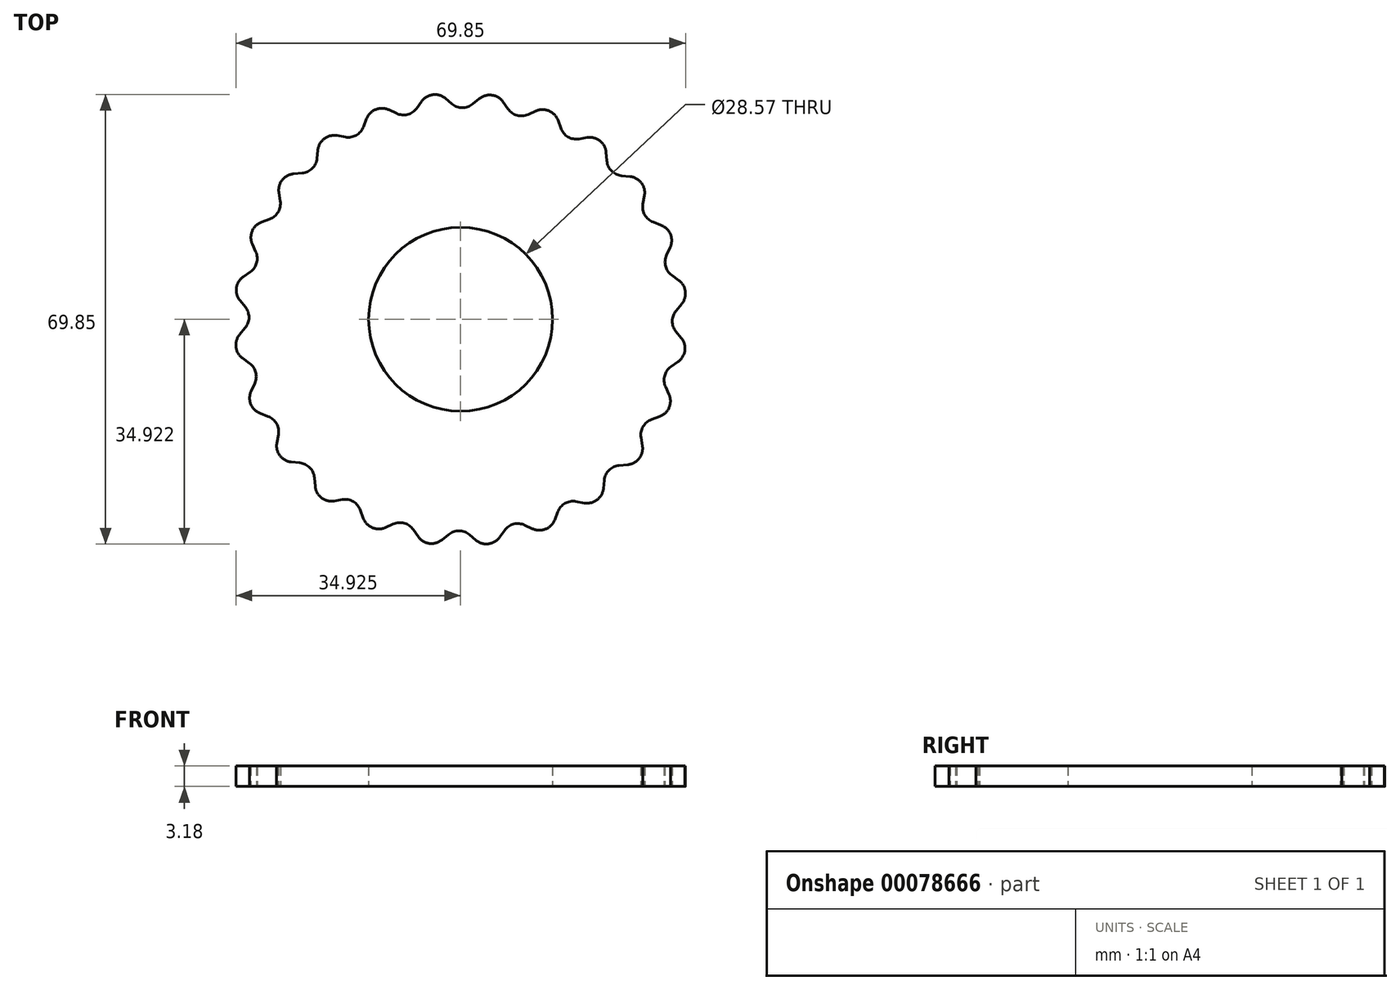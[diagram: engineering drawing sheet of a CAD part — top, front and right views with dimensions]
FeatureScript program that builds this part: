
annotation { "Feature Type Name" : "Feature", "Feature Type Description" : "" }
export const myFeature = defineFeature(function(context is Context, id is Id, definition is map)
    precondition{}
    {
        {
            var Q0;
            Q0=qCreatedBy(makeId("Top.planeOp"),FACE);
            var sketch = newSketch(context, id + "F0", { "sketchPlane" : qUnion([Q0])});
            skLineSegment(sketch, "E0", {"start": v(-103.02, 36.58) * mm, "end": v(-101.72, 36.35) * mm});
            skLineSegment(sketch, "E1", {"start": v(-98.9, 37.94) * mm, "end": v(-98.43, 39.18) * mm});
            skPoint(sketch, "E2.visualSharp", {"position": v(-99.65, 35.98) * mm});
            skArc(sketch, "E2.filletArc", {"start": v(-101.72, 36.35) * mm, "mid": v(-100.02, 36.64) * mm, "end": v(-98.9, 37.94) * mm});
            skPoint(sketch, "E3.1.0", {"position": v(-106.35, 30.93) * mm});
            skLineSegment(sketch, "E3.1.1", {"start": v(-109.76, 30.63) * mm, "end": v(-108.44, 30.75) * mm});
            skLineSegment(sketch, "E3.1.5", {"start": v(-106.13, 33.02) * mm, "end": v(-106, 34.34) * mm});
            skArc(sketch, "E3.1.6", {"start": v(-108.44, 30.75) * mm, "mid": v(-106.88, 31.47) * mm, "end": v(-106.13, 33.02) * mm});
            skPoint(sketch, "E3.2.0", {"position": v(-111.5, 24.32) * mm});
            skLineSegment(sketch, "E3.2.1", {"start": v(-114.72, 23.15) * mm, "end": v(-113.48, 23.6) * mm});
            skLineSegment(sketch, "E3.2.5", {"start": v(-111.84, 26.4) * mm, "end": v(-112.05, 27.7) * mm});
            skArc(sketch, "E3.2.6", {"start": v(-113.48, 23.6) * mm, "mid": v(-112.16, 24.7) * mm, "end": v(-111.84, 26.4) * mm});
            skPoint(sketch, "E3.3.0", {"position": v(-114.78, 16.6) * mm});
            skLineSegment(sketch, "E3.3.1", {"start": v(-117.58, 14.63) * mm, "end": v(-116.5, 15.4) * mm});
            skLineSegment(sketch, "E3.3.5", {"start": v(-115.63, 18.51) * mm, "end": v(-116.18, 19.72) * mm});
            skArc(sketch, "E3.3.6", {"start": v(-116.5, 15.4) * mm, "mid": v(-115.5, 16.8) * mm, "end": v(-115.63, 18.51) * mm});
            skPoint(sketch, "E3.4.0", {"position": v(-115.94, 8.3) * mm});
            skLineSegment(sketch, "E3.4.1", {"start": v(-118.14, 5.67) * mm, "end": v(-117.29, 6.68) * mm});
            skLineSegment(sketch, "E3.4.5", {"start": v(-117.26, 9.92) * mm, "end": v(-118.1, 10.95) * mm});
            skArc(sketch, "E3.4.6", {"start": v(-117.29, 6.68) * mm, "mid": v(-116.7, 8.3) * mm, "end": v(-117.26, 9.92) * mm});
            skPoint(sketch, "E3.5.0", {"position": v(-114.9, -0.03) * mm});
            skLineSegment(sketch, "E3.5.1", {"start": v(-116.36, -3.13) * mm, "end": v(-115.8, -1.93) * mm});
            skLineSegment(sketch, "E3.5.5", {"start": v(-116.61, 1.2) * mm, "end": v(-117.69, 1.98) * mm});
            skArc(sketch, "E3.5.6", {"start": v(-115.8, -1.93) * mm, "mid": v(-115.64, -0.22) * mm, "end": v(-116.61, 1.2) * mm});
            skPoint(sketch, "E3.6.0", {"position": v(-111.76, -7.8) * mm});
            skLineSegment(sketch, "E3.6.1", {"start": v(-112.36, -11.18) * mm, "end": v(-112.13, -9.87) * mm});
            skLineSegment(sketch, "E3.6.5", {"start": v(-113.73, -7.06) * mm, "end": v(-114.96, -6.58) * mm});
            skArc(sketch, "E3.6.6", {"start": v(-112.13, -9.87) * mm, "mid": v(-112.42, -8.18) * mm, "end": v(-113.73, -7.06) * mm});
            skPoint(sketch, "E3.7.0", {"position": v(-106.71, -14.5) * mm});
            skLineSegment(sketch, "E3.7.1", {"start": v(-106.42, -17.91) * mm, "end": v(-106.53, -16.6) * mm});
            skLineSegment(sketch, "E3.7.5", {"start": v(-108.8, -14.28) * mm, "end": v(-110.12, -14.15) * mm});
            skArc(sketch, "E3.7.6", {"start": v(-106.53, -16.6) * mm, "mid": v(-107.25, -15.03) * mm, "end": v(-108.8, -14.28) * mm});
            skPoint(sketch, "E3.8.0", {"position": v(-100.1, -19.66) * mm});
            skLineSegment(sketch, "E3.8.1", {"start": v(-98.93, -22.88) * mm, "end": v(-99.38, -21.63) * mm});
            skLineSegment(sketch, "E3.8.5", {"start": v(-102.17, -20) * mm, "end": v(-103.48, -20.2) * mm});
            skArc(sketch, "E3.8.6", {"start": v(-99.38, -21.63) * mm, "mid": v(-100.48, -20.3) * mm, "end": v(-102.17, -20) * mm});
            skPoint(sketch, "E3.9.0", {"position": v(-92.38, -22.93) * mm});
            skLineSegment(sketch, "E3.9.1", {"start": v(-90.42, -25.74) * mm, "end": v(-91.17, -24.65) * mm});
            skLineSegment(sketch, "E3.9.5", {"start": v(-94.3, -23.79) * mm, "end": v(-95.5, -24.33) * mm});
            skArc(sketch, "E3.9.6", {"start": v(-91.17, -24.65) * mm, "mid": v(-92.58, -23.66) * mm, "end": v(-94.3, -23.79) * mm});
            skPoint(sketch, "E3.10.0", {"position": v(-84.07, -24.09) * mm});
            skLineSegment(sketch, "E3.10.1", {"start": v(-81.45, -26.3) * mm, "end": v(-82.47, -25.44) * mm});
            skLineSegment(sketch, "E3.10.5", {"start": v(-85.7, -25.42) * mm, "end": v(-86.73, -26.25) * mm});
            skArc(sketch, "E3.10.6", {"start": v(-82.47, -25.44) * mm, "mid": v(-84.08, -24.85) * mm, "end": v(-85.7, -25.42) * mm});
            skPoint(sketch, "E3.11.0", {"position": v(-75.75, -23.06) * mm});
            skLineSegment(sketch, "E3.11.1", {"start": v(-72.65, -24.51) * mm, "end": v(-73.85, -23.95) * mm});
            skLineSegment(sketch, "E3.11.5", {"start": v(-76.98, -24.76) * mm, "end": v(-77.76, -25.84) * mm});
            skArc(sketch, "E3.11.6", {"start": v(-73.85, -23.95) * mm, "mid": v(-75.56, -23.8) * mm, "end": v(-76.98, -24.76) * mm});
            skPoint(sketch, "E3.12.0", {"position": v(-67.98, -19.92) * mm});
            skLineSegment(sketch, "E3.12.1", {"start": v(-64.6, -20.51) * mm, "end": v(-65.9, -20.28) * mm});
            skLineSegment(sketch, "E3.12.5", {"start": v(-68.73, -21.88) * mm, "end": v(-69.2, -23.12) * mm});
            skArc(sketch, "E3.12.6", {"start": v(-65.9, -20.28) * mm, "mid": v(-67.6, -20.57) * mm, "end": v(-68.73, -21.88) * mm});
            skPoint(sketch, "E3.13.0", {"position": v(-61.28, -14.86) * mm});
            skLineSegment(sketch, "E3.13.1", {"start": v(-57.87, -14.57) * mm, "end": v(-59.2, -14.68) * mm});
            skLineSegment(sketch, "E3.13.5", {"start": v(-61.5, -16.95) * mm, "end": v(-61.63, -18.27) * mm});
            skArc(sketch, "E3.13.6", {"start": v(-59.2, -14.68) * mm, "mid": v(-60.75, -15.4) * mm, "end": v(-61.5, -16.95) * mm});
            skPoint(sketch, "E3.14.0", {"position": v(-56.13, -8.25) * mm});
            skLineSegment(sketch, "E3.14.1", {"start": v(-52.9, -7.08) * mm, "end": v(-54.15, -7.54) * mm});
            skLineSegment(sketch, "E3.14.5", {"start": v(-55.8, -10.33) * mm, "end": v(-55.58, -11.64) * mm});
            skArc(sketch, "E3.14.6", {"start": v(-54.15, -7.54) * mm, "mid": v(-55.47, -8.64) * mm, "end": v(-55.8, -10.33) * mm});
            skPoint(sketch, "E3.15.0", {"position": v(-52.85, -0.53) * mm});
            skLineSegment(sketch, "E3.15.1", {"start": v(-50.05, 1.43) * mm, "end": v(-51.13, 0.67) * mm});
            skLineSegment(sketch, "E3.15.5", {"start": v(-52, -2.45) * mm, "end": v(-51.45, -3.66) * mm});
            skArc(sketch, "E3.15.6", {"start": v(-51.13, 0.67) * mm, "mid": v(-52.13, -0.73) * mm, "end": v(-52, -2.45) * mm});
            skPoint(sketch, "E3.16.0", {"position": v(-51.7, 7.77) * mm});
            skLineSegment(sketch, "E3.16.1", {"start": v(-49.49, 10.4) * mm, "end": v(-50.34, 9.38) * mm});
            skLineSegment(sketch, "E3.16.5", {"start": v(-50.37, 6.14) * mm, "end": v(-49.53, 5.12) * mm});
            skArc(sketch, "E3.16.6", {"start": v(-50.34, 9.38) * mm, "mid": v(-50.94, 7.77) * mm, "end": v(-50.37, 6.14) * mm});
            skPoint(sketch, "E3.17.0", {"position": v(-52.72, 16.1) * mm});
            skLineSegment(sketch, "E3.17.1", {"start": v(-51.27, 19.2) * mm, "end": v(-51.83, 18) * mm});
            skLineSegment(sketch, "E3.17.5", {"start": v(-51.02, 14.87) * mm, "end": v(-49.94, 14.09) * mm});
            skArc(sketch, "E3.17.6", {"start": v(-51.83, 18) * mm, "mid": v(-51.99, 16.29) * mm, "end": v(-51.02, 14.87) * mm});
            skLineSegment(sketch, "E4.1.18.0", {"start": v(-55.27, 27.24) * mm, "end": v(-55.5, 25.94) * mm});
            skPoint(sketch, "E4.2.18.0", {"position": v(-55.87, 23.87) * mm});
            skLineSegment(sketch, "E4.14.18.0", {"start": v(-53.9, 23.12) * mm, "end": v(-52.67, 22.65) * mm});
            skArc(sketch, "E4.17.18.0", {"start": v(-55.5, 25.94) * mm, "mid": v(-55.2, 24.24) * mm, "end": v(-53.9, 23.12) * mm});
            skLineSegment(sketch, "E4.1.19.0", {"start": v(-61.21, 33.98) * mm, "end": v(-61.1, 32.66) * mm});
            skPoint(sketch, "E4.2.19.0", {"position": v(-60.92, 30.56) * mm});
            skLineSegment(sketch, "E4.14.19.0", {"start": v(-58.83, 30.35) * mm, "end": v(-57.51, 30.21) * mm});
            skArc(sketch, "E4.17.19.0", {"start": v(-61.1, 32.66) * mm, "mid": v(-60.38, 31.1) * mm, "end": v(-58.83, 30.35) * mm});
            skLineSegment(sketch, "E4.1.20.0", {"start": v(-68.7, 38.94) * mm, "end": v(-68.25, 37.7) * mm});
            skPoint(sketch, "E4.2.20.0", {"position": v(-67.53, 35.72) * mm});
            skLineSegment(sketch, "E4.14.20.0", {"start": v(-65.46, 36.06) * mm, "end": v(-64.15, 36.27) * mm});
            skArc(sketch, "E4.17.20.0", {"start": v(-68.25, 37.7) * mm, "mid": v(-67.15, 36.37) * mm, "end": v(-65.46, 36.06) * mm});
            skLineSegment(sketch, "E4.1.21.0", {"start": v(-77.21, 41.8) * mm, "end": v(-76.45, 40.72) * mm});
            skPoint(sketch, "E4.2.21.0", {"position": v(-75.25, 39) * mm});
            skLineSegment(sketch, "E4.14.21.0", {"start": v(-73.33, 39.85) * mm, "end": v(-72.12, 40.4) * mm});
            skArc(sketch, "E4.17.21.0", {"start": v(-76.45, 40.72) * mm, "mid": v(-75.05, 39.72) * mm, "end": v(-73.33, 39.85) * mm});
            skLineSegment(sketch, "E4.1.22.0", {"start": v(-86.18, 42.36) * mm, "end": v(-85.16, 41.5) * mm});
            skPoint(sketch, "E4.2.22.0", {"position": v(-83.56, 40.15) * mm});
            skLineSegment(sketch, "E4.14.22.0", {"start": v(-81.93, 41.48) * mm, "end": v(-80.9, 42.32) * mm});
            skArc(sketch, "E4.17.22.0", {"start": v(-85.16, 41.5) * mm, "mid": v(-83.55, 40.91) * mm, "end": v(-81.93, 41.48) * mm});
            skLineSegment(sketch, "E4.1.23.0", {"start": v(-94.98, 40.58) * mm, "end": v(-93.78, 40.02) * mm});
            skPoint(sketch, "E4.2.23.0", {"position": v(-91.88, 39.13) * mm});
            skLineSegment(sketch, "E4.14.23.0", {"start": v(-90.65, 40.83) * mm, "end": v(-89.87, 41.9) * mm});
            skArc(sketch, "E4.17.23.0", {"start": v(-93.78, 40.02) * mm, "mid": v(-92.07, 39.86) * mm, "end": v(-90.65, 40.83) * mm});
            skPoint(sketch, "E5.visualSharp", {"position": v(-112.48, 30.4) * mm});
            skArc(sketch, "E5.filletArc", {"start": v(-109.76, 30.63) * mm, "mid": v(-111.54, 29.67) * mm, "end": v(-112.05, 27.7) * mm});
            skPoint(sketch, "E6.visualSharp", {"position": v(-105.72, 37.06) * mm});
            skArc(sketch, "E6.filletArc", {"start": v(-103.02, 36.58) * mm, "mid": v(-105, 36.1) * mm, "end": v(-106, 34.34) * mm});
            skPoint(sketch, "E7.visualSharp", {"position": v(-97.46, 41.74) * mm});
            skArc(sketch, "E7.filletArc", {"start": v(-94.98, 40.58) * mm, "mid": v(-97.01, 40.63) * mm, "end": v(-98.43, 39.18) * mm});
            skPoint(sketch, "E8.visualSharp", {"position": v(-88.27, 44.12) * mm});
            skArc(sketch, "E8.filletArc", {"start": v(-86.18, 42.36) * mm, "mid": v(-88.12, 42.94) * mm, "end": v(-89.87, 41.9) * mm});
            skPoint(sketch, "E9.visualSharp", {"position": v(-78.78, 44.04) * mm});
            skArc(sketch, "E9.filletArc", {"start": v(-77.21, 41.8) * mm, "mid": v(-78.94, 42.86) * mm, "end": v(-80.9, 42.32) * mm});
            skPoint(sketch, "E10.visualSharp", {"position": v(-69.63, 41.51) * mm});
            skArc(sketch, "E10.filletArc", {"start": v(-68.7, 38.94) * mm, "mid": v(-70.1, 40.41) * mm, "end": v(-72.12, 40.4) * mm});
            skPoint(sketch, "E11.visualSharp", {"position": v(-61.45, 36.7) * mm});
            skArc(sketch, "E11.filletArc", {"start": v(-61.21, 33.98) * mm, "mid": v(-62.18, 35.76) * mm, "end": v(-64.15, 36.27) * mm});
            skPoint(sketch, "E12.visualSharp", {"position": v(-54.8, 29.93) * mm});
            skArc(sketch, "E12.filletArc", {"start": v(-55.27, 27.24) * mm, "mid": v(-55.74, 29.22) * mm, "end": v(-57.51, 30.21) * mm});
            skPoint(sketch, "E13.visualSharp", {"position": v(-50.11, 21.68) * mm});
            skArc(sketch, "E13.filletArc", {"start": v(-51.27, 19.2) * mm, "mid": v(-51.22, 21.23) * mm, "end": v(-52.67, 22.65) * mm});
            skPoint(sketch, "E14.visualSharp", {"position": v(-47.73, 12.49) * mm});
            skArc(sketch, "E14.filletArc", {"start": v(-49.49, 10.4) * mm, "mid": v(-48.91, 12.34) * mm, "end": v(-49.94, 14.09) * mm});
            skPoint(sketch, "E15.visualSharp", {"position": v(-47.8, 3) * mm});
            skArc(sketch, "E15.filletArc", {"start": v(-50.05, 1.43) * mm, "mid": v(-48.98, 3.16) * mm, "end": v(-49.53, 5.12) * mm});
            skPoint(sketch, "E16.visualSharp", {"position": v(-50.34, -6.15) * mm});
            skArc(sketch, "E16.filletArc", {"start": v(-52.9, -7.08) * mm, "mid": v(-51.43, -5.69) * mm, "end": v(-51.45, -3.66) * mm});
            skPoint(sketch, "E17.visualSharp", {"position": v(-55.15, -14.33) * mm});
            skArc(sketch, "E17.filletArc", {"start": v(-57.87, -14.57) * mm, "mid": v(-56.09, -13.6) * mm, "end": v(-55.58, -11.64) * mm});
            skPoint(sketch, "E18.visualSharp", {"position": v(-61.91, -21) * mm});
            skArc(sketch, "E18.filletArc", {"start": v(-64.6, -20.51) * mm, "mid": v(-62.63, -20.04) * mm, "end": v(-61.63, -18.27) * mm});
            skPoint(sketch, "E19.visualSharp", {"position": v(-70.17, -25.67) * mm});
            skArc(sketch, "E19.filletArc", {"start": v(-72.65, -24.51) * mm, "mid": v(-70.62, -24.57) * mm, "end": v(-69.2, -23.12) * mm});
            skPoint(sketch, "E20.visualSharp", {"position": v(-79.36, -28.05) * mm});
            skArc(sketch, "E20.filletArc", {"start": v(-81.45, -26.3) * mm, "mid": v(-79.5, -26.87) * mm, "end": v(-77.76, -25.84) * mm});
            skPoint(sketch, "E21.visualSharp", {"position": v(-88.85, -27.98) * mm});
            skArc(sketch, "E21.filletArc", {"start": v(-90.42, -25.74) * mm, "mid": v(-88.69, -26.8) * mm, "end": v(-86.73, -26.25) * mm});
            skPoint(sketch, "E22.visualSharp", {"position": v(-98, -25.45) * mm});
            skArc(sketch, "E22.filletArc", {"start": v(-98.93, -22.88) * mm, "mid": v(-97.53, -24.35) * mm, "end": v(-95.5, -24.33) * mm});
            skPoint(sketch, "E23.visualSharp", {"position": v(-106.18, -20.63) * mm});
            skArc(sketch, "E23.filletArc", {"start": v(-106.42, -17.91) * mm, "mid": v(-105.45, -19.7) * mm, "end": v(-103.48, -20.2) * mm});
            skPoint(sketch, "E24.visualSharp", {"position": v(-112.84, -13.87) * mm});
            skArc(sketch, "E24.filletArc", {"start": v(-112.36, -11.18) * mm, "mid": v(-111.89, -13.15) * mm, "end": v(-110.12, -14.15) * mm});
            skPoint(sketch, "E25.visualSharp", {"position": v(-117.52, -5.61) * mm});
            skArc(sketch, "E25.filletArc", {"start": v(-116.36, -3.13) * mm, "mid": v(-116.41, -5.16) * mm, "end": v(-114.96, -6.58) * mm});
            skPoint(sketch, "E26.visualSharp", {"position": v(-119.9, 3.58) * mm});
            skArc(sketch, "E26.filletArc", {"start": v(-118.14, 5.67) * mm, "mid": v(-118.72, 3.72) * mm, "end": v(-117.69, 1.98) * mm});
            skPoint(sketch, "E27.visualSharp", {"position": v(-119.82, 13.07) * mm});
            skArc(sketch, "E27.filletArc", {"start": v(-117.58, 14.63) * mm, "mid": v(-118.64, 12.9) * mm, "end": v(-118.1, 10.95) * mm});
            skPoint(sketch, "E28.visualSharp", {"position": v(-117.3, 22.22) * mm});
            skArc(sketch, "E28.filletArc", {"start": v(-114.72, 23.15) * mm, "mid": v(-116.2, 21.75) * mm, "end": v(-116.18, 19.72) * mm});
            skCircle(sketch, "E29", {"center": v(-83.81, 8.03) * mm, "radius": 14.29 * mm});
            skSolve(sketch);
        }
        {
            var Q0;
            Q0 = qSketchRegion(id + "F0", true);
            extrude(context, id + "F1", {"entities" : qUnion([Q0]), "depth" : 3.17 * mm});
        }
    });
